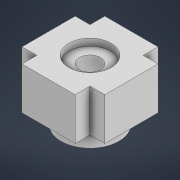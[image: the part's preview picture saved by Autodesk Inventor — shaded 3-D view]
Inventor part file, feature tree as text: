
AUTODESK INVENTOR PART (.ipt)
format: ipt  version: 2021 (Build 250183000, 183)  size: 314,880 bytes
history: native  units: mm
features: extrude x5, sketch x4, plane x1
ambient origin geometry x8: Origin, YZ Plane, XZ Plane, XY Plane, X Axis, Y Axis, Z Axis, Center Point
bodies: Volumenkörper1 (feature_tree)
feature tree (10):
  extrude  "Extrusion1"  Depth=11.75mm
  sketch  "Skizze2"  dims[d3=11.75mm d12=6.0mm d13=0.0mm]
  plane  "Arbeitsebene1"
  extrude  "Extrusion4"  Depth=6.0mm TaperAngle=0.0deg
  extrude  "Extrusion5"  Depth=6.0mm
  extrude  "Extrusion6"  Depth=2.5mm TaperAngle=0.0deg
  extrude  "Extrusion7"  Depth=2.1mm
  sketch  "Skizze1"  dims[d1=7.0mm d2=11.75mm]
  sketch  "Skizze5"  dims[d14=6.0mm d20=5.7mm]
  sketch  "Skizze6"  dims[d21=8.2mm d22=2.5mm d23=0.0mm d24=2.1mm d25=2.1mm d26=2.1mm d27=2.1mm d28=2.1mm d29=2.1mm d30=2.1mm d31=2.1mm d32=6.0mm d33=0.0mm d34=1.0mm d35=0.0mm d38=3.0mm d39=10.0mm d40=0.0mm d15=0.5mm d16=0.872665mm d17=0.5mm d18=0.872665mm d36=0.5mm d37=0.872665mm]
